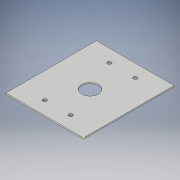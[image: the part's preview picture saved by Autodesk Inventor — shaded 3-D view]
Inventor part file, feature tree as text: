
AUTODESK INVENTOR PART (.ipt)
format: ipt  version: 2019 (Build 230136000, 136)  size: 108,032 bytes
history: native  units: mm
features: sketch x3, extrude x2
ambient origin geometry x8: Origin, YZ Plane, XZ Plane, XY Plane, X Axis, Y Axis, Z Axis, Center Point
bodies: Solid1 (feature_tree)
feature tree (5):
  extrude  "Extrusion1"  Depth=70.0mm
  extrude  "Extrusion2"  Depth=1.0mm
  sketch  "Sketch3"  dims[d5=3.0mm d6=3.0mm d7=3.0mm d8=13.0mm d9=1.0mm d10=0.0mm]
  sketch  "Sketch1"  dims[d0=60.0mm d1=70.0mm]
  sketch  "Sketch2"  dims[d2=1.0mm d3=0.0mm d4=3.0mm]
